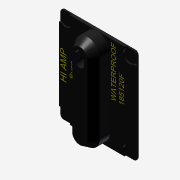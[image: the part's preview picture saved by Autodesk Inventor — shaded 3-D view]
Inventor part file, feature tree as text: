
AUTODESK INVENTOR PART (.ipt)
format: ipt  version: 2016 SP1 (Build 200210100, 210)  size: 661,504 bytes
history: native  units: mm (DEFAULTED — no unit token found)
features: sketch x6, extrude x4, plane x2, mirror x2, emboss x2, chamfer x1, reference x1
ambient origin geometry x8: Origin, YZ Plane, XZ Plane, XY Plane, X Axis, Y Axis, Z Axis, Center Point
bodies: Solid1 (feature_tree)
feature tree (18):
  extrude  "Extrusion1"  Depth=6.35mm
  extrude  "Extrusion2"  Depth=2.54mm
  chamfer  "Chamfer2"  Distance=8.89mm
  extrude  "Extrusion3"  Depth=0.762mm
  plane  "Work Plane1"
  plane  "Work Plane2"
  extrude  "Extrusion5"  Depth=0.0508mm TaperAngle=0.0deg
  mirror  "Mirror3"
  mirror  "Mirror4"
  emboss  "Emboss1"
  emboss  "Emboss2"
  sketch  "Sketch1"  dims[d0=1.524mm d1=0.0mm d2=6.35mm]
  reference  "Reference1"
  sketch  "Sketch2"  dims[d3=8.89mm d4=0.0mm d7=3.81mm d8=2.54mm]
  sketch  "Sketch3"  dims[d10=2.159mm]
  sketch  "Sketch5"  dims[d11=7.62mm d12=8.89mm d13=0.0mm]
  sketch  "Sketch6"  dims[d17=6.35mm d18=0.762mm]
  sketch  "Sketch7"  dims[d19=0.762mm d20=0.762mm d21=0.0mm d22=0.0508mm d23=0.0mm d24=0.0508mm d25=0.0mm d26=45.0deg]
